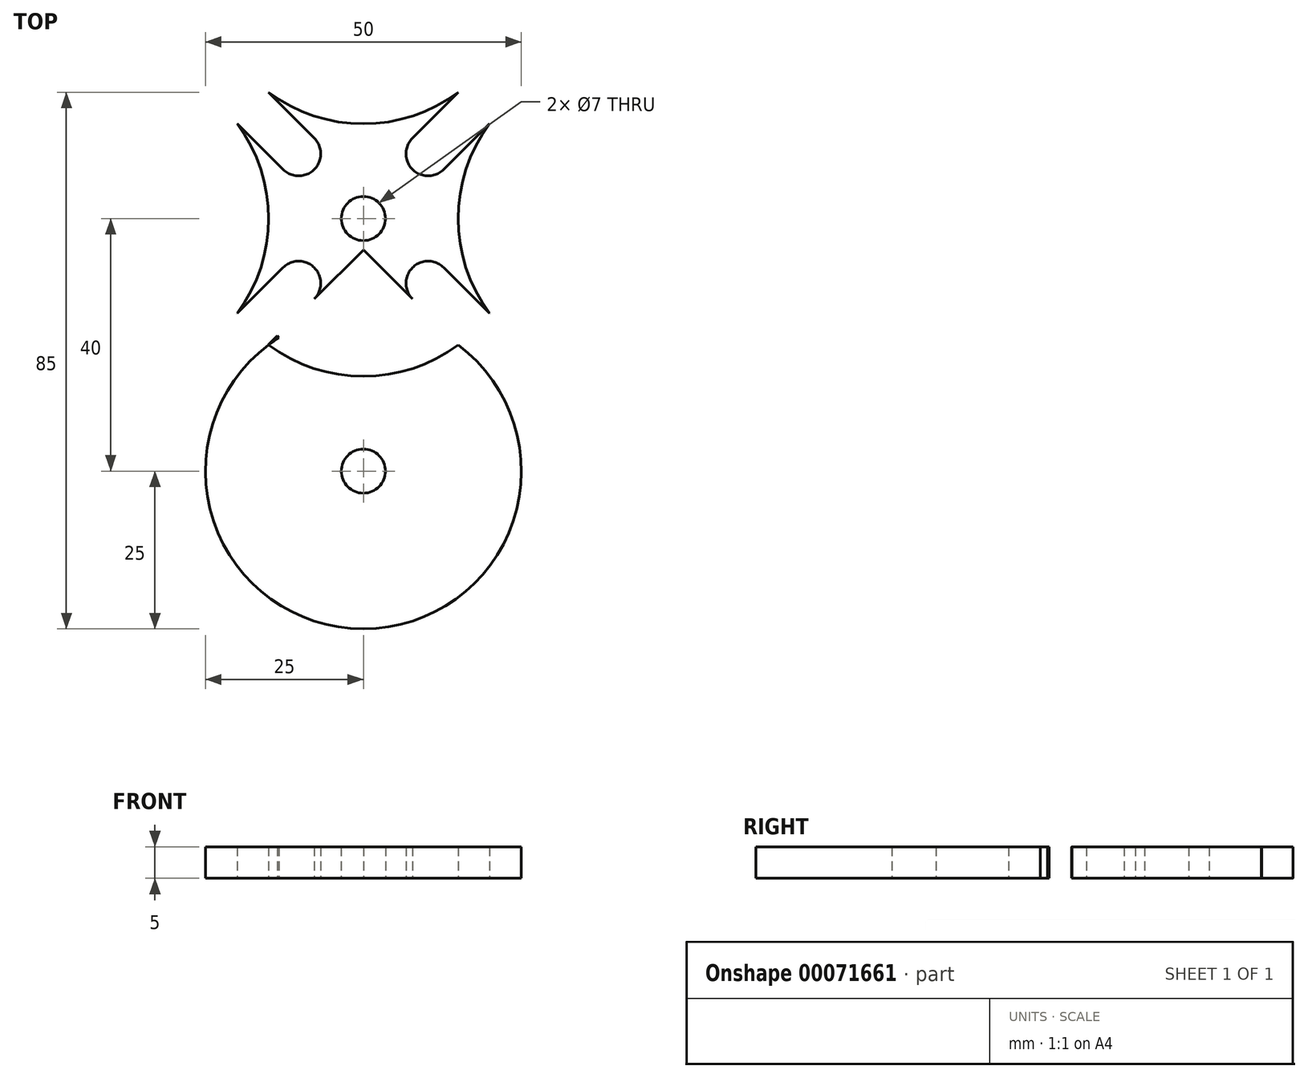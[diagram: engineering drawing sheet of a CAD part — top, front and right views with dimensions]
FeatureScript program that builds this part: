
annotation { "Feature Type Name" : "Feature", "Feature Type Description" : "" }
export const myFeature = defineFeature(function(context is Context, id is Id, definition is map)
    precondition{}
    {
        {
            var Q0;
            Q0=qCreatedBy(makeId("Top.planeOp"),FACE);
            var sketch = newSketch(context, id + "F0", { "sketchPlane" : qUnion([Q0])});
            skArc(sketch, "E0", {"start": v(-15, 20) * mm, "mid": v(0, -25) * mm, "end": v(15, 20) * mm});
            skArc(sketch, "E1", {"start": v(15, 20) * mm, "mid": v(0, 25) * mm, "end": v(-15, 20) * mm});
            skArc(sketch, "E2.1.0", {"start": v(20, 55) * mm, "mid": v(15, 40) * mm, "end": v(20, 25) * mm});
            skArc(sketch, "E2.2.0", {"start": v(-15, 60) * mm, "mid": v(0, 55) * mm, "end": v(15, 60) * mm});
            skArc(sketch, "E2.3.0", {"start": v(-20, 25) * mm, "mid": v(-15, 40) * mm, "end": v(-20, 55) * mm});
            skPoint(sketch, "E2.center", {"position": v(0, 40) * mm});
            skLineSegment(sketch, "E3", {"start": v(-19.98, 24.97) * mm, "end": v(15.03, 59.98) * mm});
            skLineSegment(sketch, "E4", {"start": v(-19.98, 55.03) * mm, "end": v(15.03, 20.02) * mm});
            skLineSegment(sketch, "E5", {"start": v(19.98, 24.97) * mm, "end": v(-15.03, 59.98) * mm});
            skLineSegment(sketch, "E6", {"start": v(19.98, 55.03) * mm, "end": v(-15.03, 20.02) * mm});
            skLineSegment(sketch, "E7", {"start": v(0, 44.95) * mm, "end": v(0, 35.05) * mm, "construction": true});
            skArc(sketch, "E8", {"start": v(-7.78, 27.27) * mm, "mid": v(-7.78, 32.22) * mm, "end": v(-12.73, 32.22) * mm});
            skArc(sketch, "E9", {"start": v(-12.73, 47.78) * mm, "mid": v(-7.78, 47.78) * mm, "end": v(-7.78, 52.73) * mm});
            skArc(sketch, "E10", {"start": v(7.78, 52.73) * mm, "mid": v(7.78, 47.78) * mm, "end": v(12.73, 47.78) * mm});
            skArc(sketch, "E11", {"start": v(12.73, 32.22) * mm, "mid": v(7.78, 32.22) * mm, "end": v(7.78, 27.27) * mm});
            skCircle(sketch, "E12", {"center": v(0, 40) * mm, "radius": 3.5 * mm});
            skCircle(sketch, "E13", {"center": v(0, 0) * mm, "radius": 3.5 * mm});
            skCircle(sketch, "E14", {"center": v(0, 40) * mm, "radius": 11 * mm, "construction": true});
            skLineSegment(sketch, "E15", {"start": v(0, 40) * mm, "end": v(-17.68, 22.32) * mm, "construction": true});
            skCircle(sketch, "E16", {"center": v(-17.68, 22.32) * mm, "radius": 2.5 * mm});
            skArc(sketch, "E17", {"start": v(-15, 20) * mm, "mid": v(0, 15) * mm, "end": v(15, 20) * mm});
            skArc(sketch, "E18", {"start": v(15, 20) * mm, "mid": v(0, 65) * mm, "end": v(-15, 20) * mm});
            skLineSegment(sketch, "E19", {"start": v(-19.7, 20.84) * mm, "end": v(-2.82, -2.08) * mm});
            skLineSegment(sketch, "E20", {"start": v(-15.77, 23.94) * mm, "end": v(2.67, 2.27) * mm});
            skLineSegment(sketch, "E21", {"start": v(-17.68, 22.32) * mm, "end": v(0, 0) * mm, "construction": true});
            skSolve(sketch);
        }
        {
            var Q0;
            {var subQ0=sQuery(id+"F0.wireOp",EDGE,"E2.3.0");Q0=makeQuery(id+"F0.imprint","IMPRINT",FACE,{"disambiguationData":[TD([[makeQuery(id+"F0.imprint","IMPRINT",EDGE,{"derivedFrom":subQ0}),-1.0]])]});}
            var Q1;
            {var subQ4=sQuery(id+"F0.wireOp",EDGE,"E2.2.0");Q1=makeQuery(id+"F0.imprint","IMPRINT",FACE,{"disambiguationData":[TD([[makeQuery(id+"F0.imprint","IMPRINT",EDGE,{"derivedFrom":subQ4}),-1.0]])]});}
            var Q2;
            {var subQ5=sQuery(id+"F0.wireOp",EDGE,"E9");Q2=makeQuery(id+"F0.imprint","IMPRINT",FACE,{"disambiguationData":[TD([[makeQuery(id+"F0.imprint","IMPRINT",EDGE,{"derivedFrom":subQ5}),-1.0]])]});}
            var Q3;
            {var subQ0=sQuery(id+"F0.wireOp",EDGE,"E10");Q3=makeQuery(id+"F0.imprint","IMPRINT",FACE,{"disambiguationData":[TD([[makeQuery(id+"F0.imprint","IMPRINT",EDGE,{"derivedFrom":subQ0}),-1.0]])]});}
            var Q4;
            {var subQ0=sQuery(id+"F0.wireOp",EDGE,"E11");Q4=makeQuery(id+"F0.imprint","IMPRINT",FACE,{"disambiguationData":[TD([[makeQuery(id+"F0.imprint","IMPRINT",EDGE,{"derivedFrom":subQ0}),-1.0]])]});}
            var Q5;
            {var subQ0=sQuery(id+"F0.wireOp",EDGE,"E8");Q5=makeQuery(id+"F0.imprint","IMPRINT",FACE,{"disambiguationData":[TD([[makeQuery(id+"F0.imprint","IMPRINT",EDGE,{"derivedFrom":subQ0}),-1.0]])]});}
            var Q6;
            {var subQ0=sQuery(id+"F0.wireOp",EDGE,"E4");var subQ1=sQuery(id+"F0.wireOp",EDGE,"E3");var subQ2=makeQuery(id+"F0.imprint","INTERSECT",VERTEX,{"derivedFrom":[subQ1,subQ0]});Q6=makeQuery(id+"F0.imprint","IMPRINT",FACE,{"disambiguationData":[TD([[makeQuery(id+"F0.imprint","IMPRINT",EDGE,{"disambiguationData":[TD([[subQ2,-1.0]])],"derivedFrom":subQ1}),-1.0]])]});}
            var Q7;
            {var subQ0=sQuery(id+"F0.wireOp",EDGE,"E1");Q7=makeQuery(id+"F0.imprint","IMPRINT",FACE,{"disambiguationData":[TD([[makeQuery(id+"F0.imprint","IMPRINT",EDGE,{"derivedFrom":subQ0}),-1.0]])]});}
            var Q8;
            {var subQ7=sQuery(id+"F0.wireOp",EDGE,"E2.1.0");Q8=makeQuery(id+"F0.imprint","IMPRINT",FACE,{"disambiguationData":[TD([[makeQuery(id+"F0.imprint","IMPRINT",EDGE,{"derivedFrom":subQ7}),-1.0]])]});}
            var Q9;
            {var subQ1=sQuery(id+"F0.wireOp",EDGE,"E0");Q9=makeQuery(id+"F0.imprint","IMPRINT",FACE,{"disambiguationData":[TD([[makeQuery(id+"F0.imprint","IMPRINT",EDGE,{"derivedFrom":subQ1}),1.0]])]});}
            var Q10;
            {var subQ0=sQuery(id+"F0.wireOp",EDGE,"E6");var subQ1=sQuery(id+"F0.wireOp",EDGE,"E5");var subQ2=makeQuery(id+"F0.imprint","INTERSECT",VERTEX,{"derivedFrom":[subQ1,subQ0]});Q10=makeQuery(id+"F0.imprint","IMPRINT",FACE,{"disambiguationData":[TD([[makeQuery(id+"F0.imprint","IMPRINT",EDGE,{"disambiguationData":[TD([[subQ2,-1.0]])],"derivedFrom":subQ1}),1.0]])]});}
            var Q11;
            {var subQ0=sQuery(id+"F0.wireOp",EDGE,"E12");var subQ1=sQuery(id+"F0.wireOp",EDGE,"E3");var subQ2=makeQuery(id+"F0.imprint","INTERSECT",VERTEX,{"derivedFrom":[subQ1,subQ0]});Q11=makeQuery(id+"F0.imprint","IMPRINT",FACE,{"disambiguationData":[TD([[makeQuery(id+"F0.imprint","IMPRINT",EDGE,{"disambiguationData":[TD([[subQ2,-1.0]])],"derivedFrom":subQ1}),-1.0]])]});}
            var Q12;
            {var subQ0=sQuery(id+"F0.wireOp",EDGE,"E12");var subQ1=sQuery(id+"F0.wireOp",EDGE,"E4");var subQ2=makeQuery(id+"F0.imprint","INTERSECT",VERTEX,{"derivedFrom":[subQ1,subQ0]});Q12=makeQuery(id+"F0.imprint","IMPRINT",FACE,{"disambiguationData":[TD([[makeQuery(id+"F0.imprint","IMPRINT",EDGE,{"disambiguationData":[TD([[subQ2,-1.0]])],"derivedFrom":subQ1}),1.0]])]});}
            var Q13;
            {var subQ0=sQuery(id+"F0.wireOp",EDGE,"2021f431-e942-49c2-8635-e36a2d9a4bb1");var subQ1=sQuery(id+"F0.wireOp",EDGE,"E1");var subQ2=makeQuery(id+"F0.imprint","INTERSECT",VERTEX,{"disambiguationData":[OD(0.0)],"derivedFrom":[subQ1,subQ0]});Q13=makeQuery(id+"F0.imprint","IMPRINT",FACE,{"disambiguationData":[TD([[makeQuery(id+"F0.imprint","IMPRINT",EDGE,{"disambiguationData":[TD([[subQ2,-1.0]])],"derivedFrom":subQ1}),-1.0]])]});}
            extrude(context, id + "F1", {"entities" : qUnion([Q0, Q1, Q2, Q3, Q4, Q5, Q6, Q7, Q8, Q9, Q10, Q11, Q12, Q13]), "depth" : 5 * mm});
        }
    });
